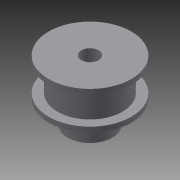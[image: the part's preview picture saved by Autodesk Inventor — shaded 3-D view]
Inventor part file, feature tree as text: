
AUTODESK INVENTOR PART (.ipt)
format: ipt  version: 2015 (Build 190159000, 159)  size: 113,664 bytes
history: native  units: mm
features: sketch x2, revolve x1, hole x1
ambient origin geometry x8: Origin, YZ Plane, XZ Plane, XY Plane, X Axis, Y Axis, Z Axis, Center Point
bodies: Solid1 (feature_tree)
feature tree (4):
  revolve  "Revolution1"  [1 undecoded]
  hole  "Hole1"  [1 undecoded]
  sketch  "Sketch1"  dims[d0=24.0mm d1=17.5mm]
  sketch  "Sketch2"  dims[d2=8.0mm d3=11.0mm d4=5.0mm d5=13.0mm d6=18.89mm d7=90.0deg d8=3.0mm d9=2.459mm d10=6.0mm d11=4.0mm d12=2.0mm d13=90.0deg d14=8.0mm d15=20.594885mm]
note: 2 required parameter values undecoded (feature->parameter linkage not recoverable at this tier; creation-order binding heuristic only, values carry confidence <= 0.55)